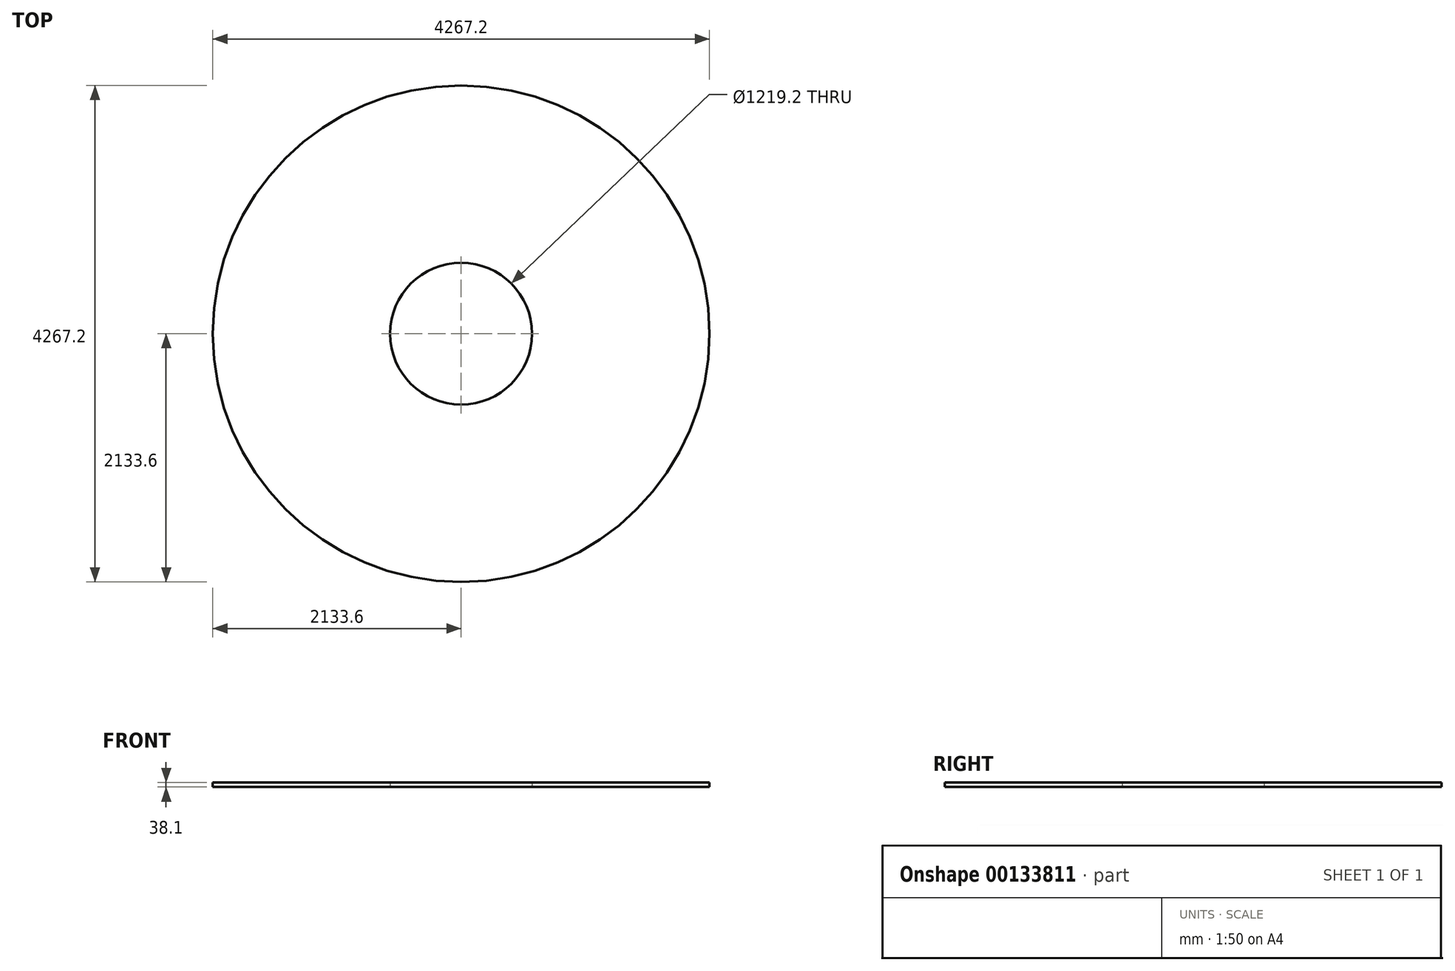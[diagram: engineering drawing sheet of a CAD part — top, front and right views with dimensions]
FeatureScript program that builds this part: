
annotation { "Feature Type Name" : "Feature", "Feature Type Description" : "" }
export const myFeature = defineFeature(function(context is Context, id is Id, definition is map)
    precondition{}
    {
        {
            var Q0;
            Q0=qCreatedBy(makeId("Top.planeOp"),FACE);
            var sketch = newSketch(context, id + "F0", { "sketchPlane" : qUnion([Q0])});
            skCircle(sketch, "E0", {"center": v(0, 0) * mm, "radius": 2133.6 * mm});
            skSolve(sketch);
        }
        {
            var Q0;
            Q0=makeQuery(id+"F0.imprint","IMPRINT",FACE,{"disambiguationData":[TD([[makeQuery(id+"F0.imprint","IMPRINT",EDGE,{"derivedFrom":sQuery(id+"F0.wireOp",EDGE,"E0")}),1.0]])]});
            var sketch = newSketch(context, id + "F1", { "sketchPlane" : qUnion([Q0])});
            skCircle(sketch, "E1", {"center": v(0, 0) * mm, "radius": 609.6 * mm});
            skSolve(sketch);
        }
        {
            var Q0;
            Q0 = qSketchRegion(id + "F0", true);
            extrude(context, id + "F2", {"entities" : qUnion([Q0]), "depth" : 38.1 * mm});
        }
        {
            var Q0;
            Q0=sQuery(id+"F1.wireOp",VERTEX,"E1.center");
            var Q1;
            Q1=makeQuery(id+"F2.opExtrude","SWEPT_BODY",BODY,{"disambiguationData":[OSD([sQuery(id+"F0.wireOp",EDGE,"E0")])]});
            hole(context, id + "F3", {"style" : HoleStyle.SIMPLE, "endStyle" : HoleEndStyle.THROUGH, "oppositeDirection" : true, "holeDiameter" : 1219.2 * mm, "locations" : qUnion([Q0]), "scope" : qUnion([Q1]), "isTappedThrough" : true});
        }
    });
